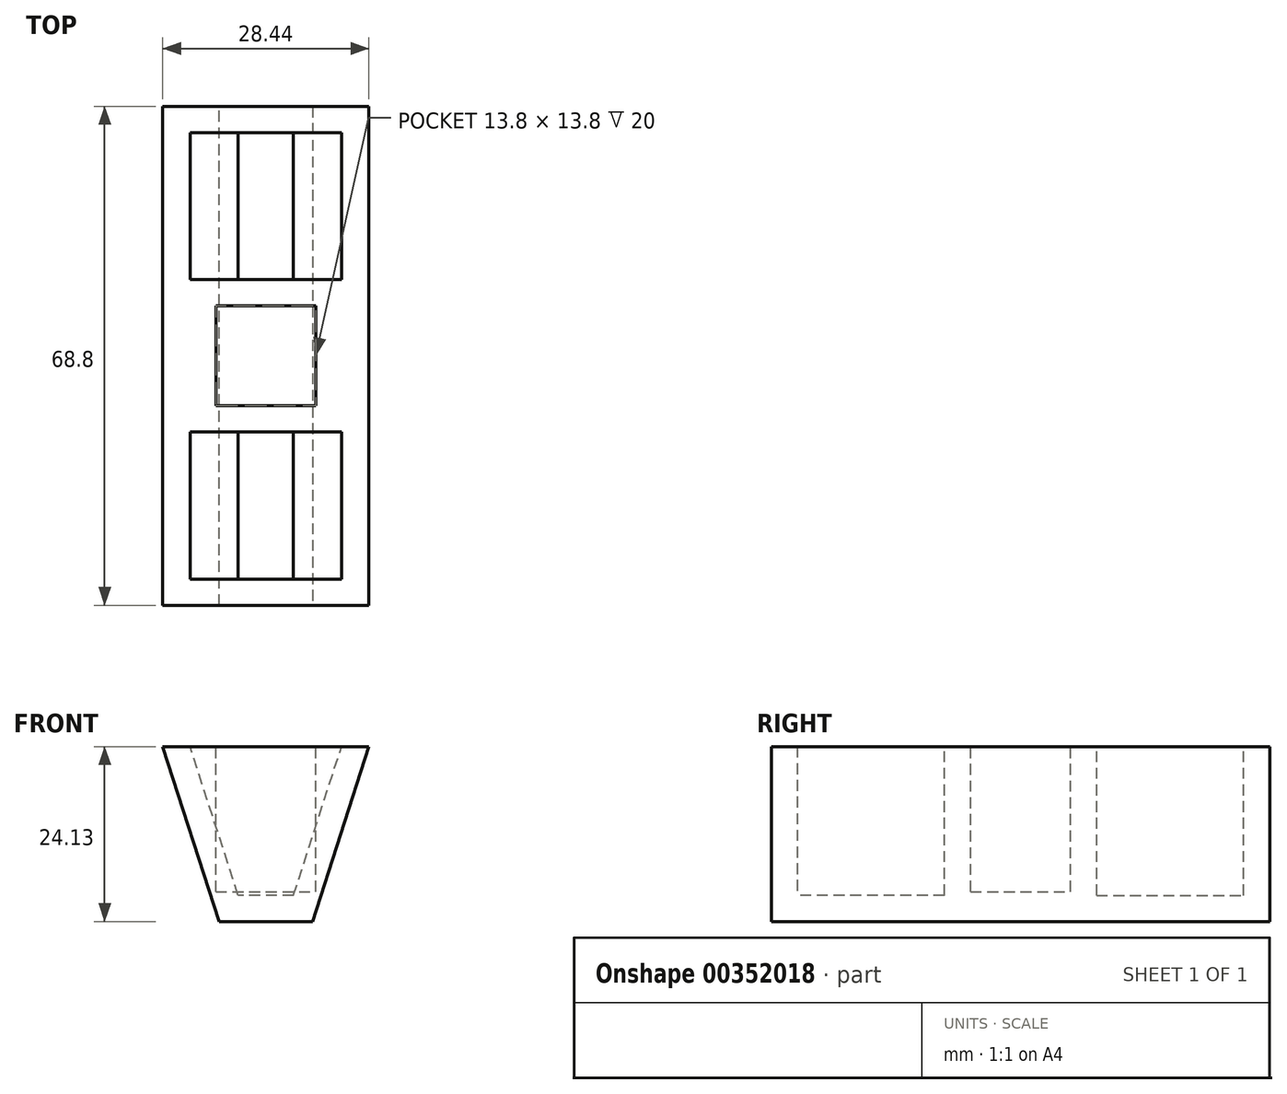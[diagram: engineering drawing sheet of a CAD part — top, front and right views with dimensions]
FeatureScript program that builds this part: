
annotation { "Feature Type Name" : "Feature", "Feature Type Description" : "" }
export const myFeature = defineFeature(function(context is Context, id is Id, definition is map)
    precondition{}
    {
        {
            var Q0;
            Q0=qCreatedBy(makeId("Top.planeOp"),FACE);
            cPlane(context, id + "F0", {"entities" : qUnion([Q0]), "cplaneType" : CPlaneType.OFFSET, "offset" : 36.12 * mm, "width" : 150 * mm, "height" : 150 * mm});
        }
        {
            var Q0;
            Q0=qCreatedBy(id+"F0.planeOp",FACE);
            var sketch = newSketch(context, id + "F1", { "sketchPlane" : qUnion([Q0])});
            skLineSegment(sketch, "E0", {"start": v(-18.1, 0) * mm, "end": v(-18.1, -68.8) * mm});
            skLineSegment(sketch, "E1", {"start": v(-18.1, -68.8) * mm, "end": v(18.1, -68.8) * mm});
            skLineSegment(sketch, "E2", {"start": v(18.1, -68.8) * mm, "end": v(18.1, 0) * mm});
            skLineSegment(sketch, "E3", {"start": v(-18.1, 0) * mm, "end": v(18.1, 0) * mm});
            skSolve(sketch);
        }
        {
            var Q0;
            Q0=qCreatedBy(makeId("Top.planeOp"),FACE);
            var sketch = newSketch(context, id + "F2", { "sketchPlane" : qUnion([Q0])});
            skLineSegment(sketch, "E4", {"start": v(6.43, 0) * mm, "end": v(6.43, -68.8) * mm});
            skLineSegment(sketch, "E5", {"start": v(6.43, -68.8) * mm, "end": v(-6.43, -68.8) * mm});
            skLineSegment(sketch, "E6", {"start": v(-6.43, -68.8) * mm, "end": v(-6.43, 0) * mm});
            skLineSegment(sketch, "E7", {"start": v(-6.43, 0) * mm, "end": v(6.43, 0) * mm});
            skSolve(sketch);
        }
        {
            var Q0;
            Q0=makeQuery(id+"F1.imprint","IMPRINT",FACE,{"disambiguationData":[TD([[makeQuery(id+"F1.imprint","IMPRINT",EDGE,{"derivedFrom":sQuery(id+"F1.wireOp",EDGE,"E0")}),1.0]])]});
            var Q1;
            Q1=makeQuery(id+"F2.imprint","IMPRINT",FACE,{"disambiguationData":[TD([[makeQuery(id+"F2.imprint","IMPRINT",EDGE,{"derivedFrom":sQuery(id+"F2.wireOp",EDGE,"E4")}),-1.0]])]});
            loft(context, id + "F3", {"sheetProfilesArray" : [{ "sheetProfileEntities" : qUnion([Q0]) }, { "sheetProfileEntities" : qUnion([Q1]) }]});
        }
        {
            var Q0;
            Q0=makeQuery(id+"F3.opLoft","CAP_FACE",FACE,{"disambiguationData":[OSD([makeQuery(id+"F1.imprint","IMPRINT",FACE,{"disambiguationData":[TD([[makeQuery(id+"F1.imprint","IMPRINT",EDGE,{"derivedFrom":sQuery(id+"F1.wireOp",EDGE,"E0")}),1.0]])]})])],"isStart":true});
            extrude(context, id + "F4", {"entities" : qUnion([Q0]), "operationType" : NewBodyOperationType.REMOVE, "oppositeDirection" : true, "depth" : 12 * mm});
        }
        {
            var Q0;
            Q0=qCreatedBy(id+"F0.planeOp",FACE);
            var sketch = newSketch(context, id + "F5", { "sketchPlane" : qUnion([Q0])});
            skLineSegment(sketch, "E8", {"start": v(-6.9, -27.5) * mm, "end": v(6.9, -27.5) * mm});
            skLineSegment(sketch, "E9", {"start": v(6.9, -27.5) * mm, "end": v(6.9, -41.3) * mm});
            skLineSegment(sketch, "E10", {"start": v(6.9, -41.3) * mm, "end": v(-6.9, -41.3) * mm});
            skLineSegment(sketch, "E11", {"start": v(-6.9, -41.3) * mm, "end": v(-6.9, -27.5) * mm});
            skSolve(sketch);
        }
        {
            var Q0;
            Q0=makeQuery(id+"F5.imprint","IMPRINT",FACE,{"disambiguationData":[TD([[makeQuery(id+"F5.imprint","IMPRINT",EDGE,{"derivedFrom":sQuery(id+"F5.wireOp",EDGE,"E8")}),-1.0]])]});
            extrude(context, id + "F6", {"entities" : qUnion([Q0]), "operationType" : NewBodyOperationType.REMOVE, "oppositeDirection" : true, "depth" : 32 * mm});
        }
        {
            var Q0;
            Q0=makeQuery(id+"F4.boolean.opBoolean","COPY",FACE,{"derivedFrom":makeQuery(id+"F4.opExtrude","CAP_FACE",FACE,{"disambiguationData":[OSD([makeQuery(id+"F1.imprint","IMPRINT",FACE,{"disambiguationData":[TD([[makeQuery(id+"F1.imprint","IMPRINT",EDGE,{"derivedFrom":sQuery(id+"F1.wireOp",EDGE,"E0")}),1.0]])]})])],"isStart":false})});
            shell(context, id + "F7", {"entities" : qUnion([Q0]), "thickness" : 3.6 * mm});
        }
    });
